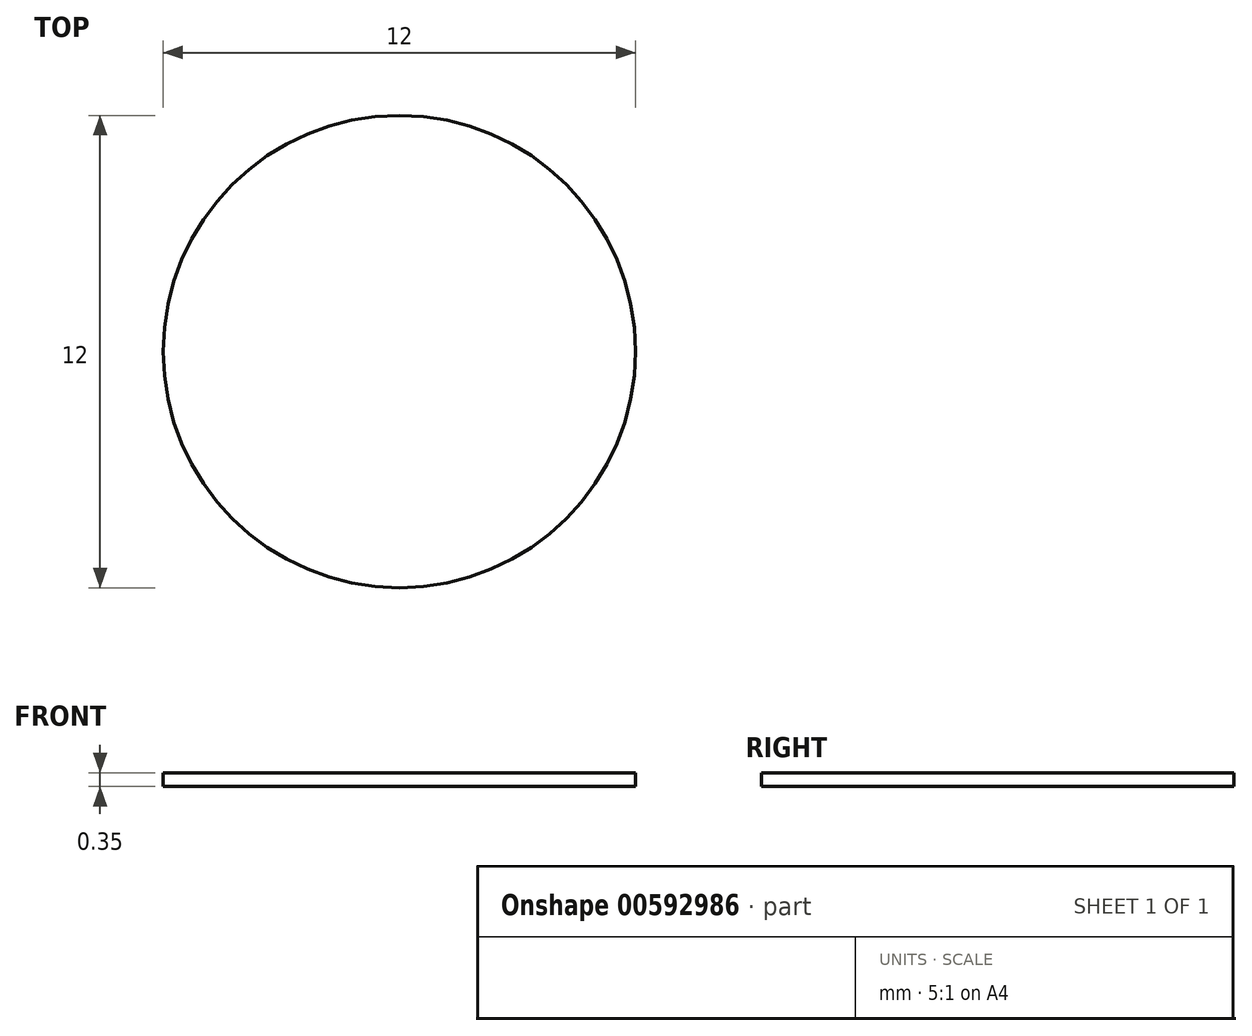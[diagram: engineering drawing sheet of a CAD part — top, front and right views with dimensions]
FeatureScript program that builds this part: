
annotation { "Feature Type Name" : "Feature", "Feature Type Description" : "" }
export const myFeature = defineFeature(function(context is Context, id is Id, definition is map)
    precondition{}
    {
        {
            var Q0;
            Q0=qCreatedBy(makeId("Top.planeOp"),FACE);
            var sketch = newSketch(context, id + "F0", { "sketchPlane" : qUnion([Q0])});
            skCircle(sketch, "E0", {"center": v(0, 0) * mm, "radius": 6 * mm});
            skSolve(sketch);
        }
        {
            var Q0;
            Q0=makeQuery(id+"F0.imprint","IMPRINT",FACE,{"disambiguationData":[TD([[makeQuery(id+"F0.imprint","IMPRINT",EDGE,{"derivedFrom":sQuery(id+"F0.wireOp",EDGE,"E0")}),1.0]])]});
            var Q1;
            Q1=makeQuery(id+"F0.imprint","IMPRINT",FACE,{"disambiguationData":[TD([[makeQuery(id+"F0.imprint","IMPRINT",EDGE,{"derivedFrom":sQuery(id+"F0.wireOp",EDGE,"TuVyb0dA-HN1L-bcHI-Ftj1-qyrcgxnZELIL")}),1.0]])]});
            extrude(context, id + "F1", {"entities" : qUnion([Q0, Q1]), "oppositeDirection" : true, "depth" : 0.35 * mm, "offsetDistance" : 25 * mm});
        }
    });
